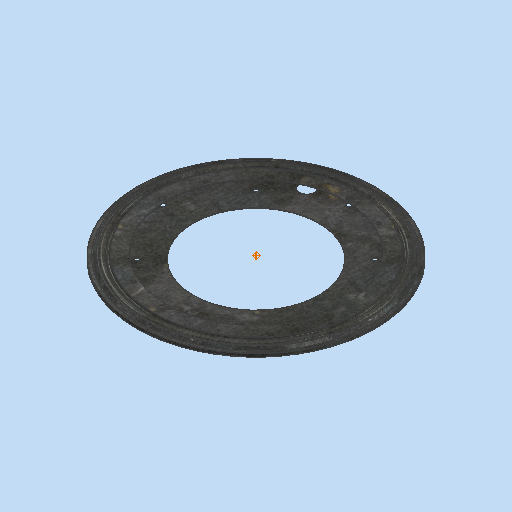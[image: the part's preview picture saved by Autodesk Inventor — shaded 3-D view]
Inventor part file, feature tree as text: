
AUTODESK INVENTOR PART (.ipt)
format: ipt  version: 2024 (Build 280153000, 153)  size: 937,984 bytes
history: native  units: in
note: dims shown in document units (in); Inventor stores cm internally (conversion verified against a paired STEP export)
features: other x17, revolve x1
ambient origin geometry x8: Origin, YZ Plane, XZ Plane, XY Plane, X Axis, Y Axis, Z Axis, Center Point
bodies: Solid1 (feature_tree), Solid2 (feature_tree), Solid3 (feature_tree), Solid4 (feature_tree), Solid5 (feature_tree), Solid6 (feature_tree), Solid7 (feature_tree), Solid8 (feature_tree), Solid9 (feature_tree), Solid10 (feature_tree), Solid11 (feature_tree), Solid12 (feature_tree), Solid13 (feature_tree), Solid14 (feature_tree), Solid15 (feature_tree), Solid16 (feature_tree), Solid17 (feature_tree), Solid18 (feature_tree)
feature tree (18):
  revolve  "Revolve1"  [1 undecoded]
  other  "CirPattern5[1]"
  other  "CirPattern5[2]"
  other  "CirPattern5[3]"
  other  "CirPattern5[4]"
  other  "CirPattern5[5]"
  other  "CirPattern5[6]"
  other  "CirPattern5[7]"
  other  "CirPattern5[8]"
  other  "Cut-Extrude5[1]"
  other  "Cut-Extrude5[2]"
  other  "Cut-Extrude5[3]"
  other  "Cut-Extrude5[4]"
  other  "Cut-Extrude5[5]"
  other  "Cut-Extrude6"
  other  "CirPattern5[9]"
  other  "CirPattern5[10]"
  other  "CirPattern5[11]"
note: 1 required parameter value undecoded (feature->parameter linkage not recoverable at this tier; creation-order binding heuristic only, values carry confidence <= 0.55)
